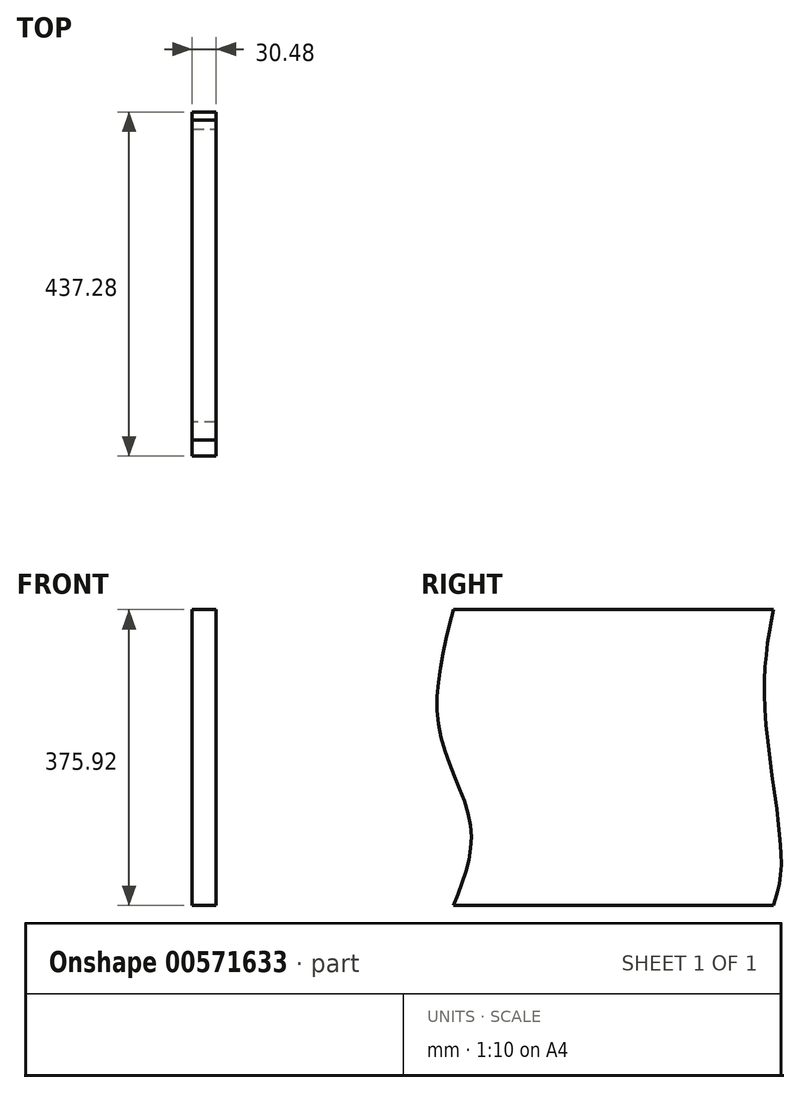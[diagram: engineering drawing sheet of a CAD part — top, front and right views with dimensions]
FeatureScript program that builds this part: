
annotation { "Feature Type Name" : "Feature", "Feature Type Description" : "" }
export const myFeature = defineFeature(function(context is Context, id is Id, definition is map)
    precondition{}
    {
        {
            var Q0;
            Q0=qCreatedBy(makeId("Right.planeOp"),FACE);
            var sketch = newSketch(context, id + "F0", { "sketchPlane" : qUnion([Q0])});
            skLineSegment(sketch, "E0.bottom", {"start": v(0, 0) * mm, "end": v(406.4, 0) * mm});
            skLineSegment(sketch, "E0.top", {"start": v(0, -375.92) * mm, "end": v(406.4, -375.92) * mm});
            skFitSpline(sketch, "E1", {"points": [v(0, 0) * mm, v(-17.98, -152.1) * mm, v(21.98, -275.61) * mm, v(0, -375.92) * mm], "startDerivative": vector(-110.14, -428) * mm, "endDerivative": vector(-132.03, -330.53) * mm});
            skFitSpline(sketch, "E2", {"points": [v(406.4, 0) * mm, v(395.4, -121.6) * mm, v(416.47, -319.93) * mm, v(406.4, -375.92) * mm], "startDerivative": vector(-59.5, -318.94) * mm, "endDerivative": vector(-65.75, -196.02) * mm});
            skSolve(sketch);
        }
        {
            var Q0;
            Q0=makeQuery(id+"F0.imprint","IMPRINT",FACE,{"disambiguationData":[TD([[makeQuery(id+"F0.imprint","IMPRINT",EDGE,{"derivedFrom":sQuery(id+"F0.wireOp",EDGE,"E0.bottom")}),-1.0]])]});
            extrude(context, id + "F1", {"entities" : qUnion([Q0]), "depth" : 30.48 * mm, "offsetDistance" : 25.4 * mm});
        }
    });
